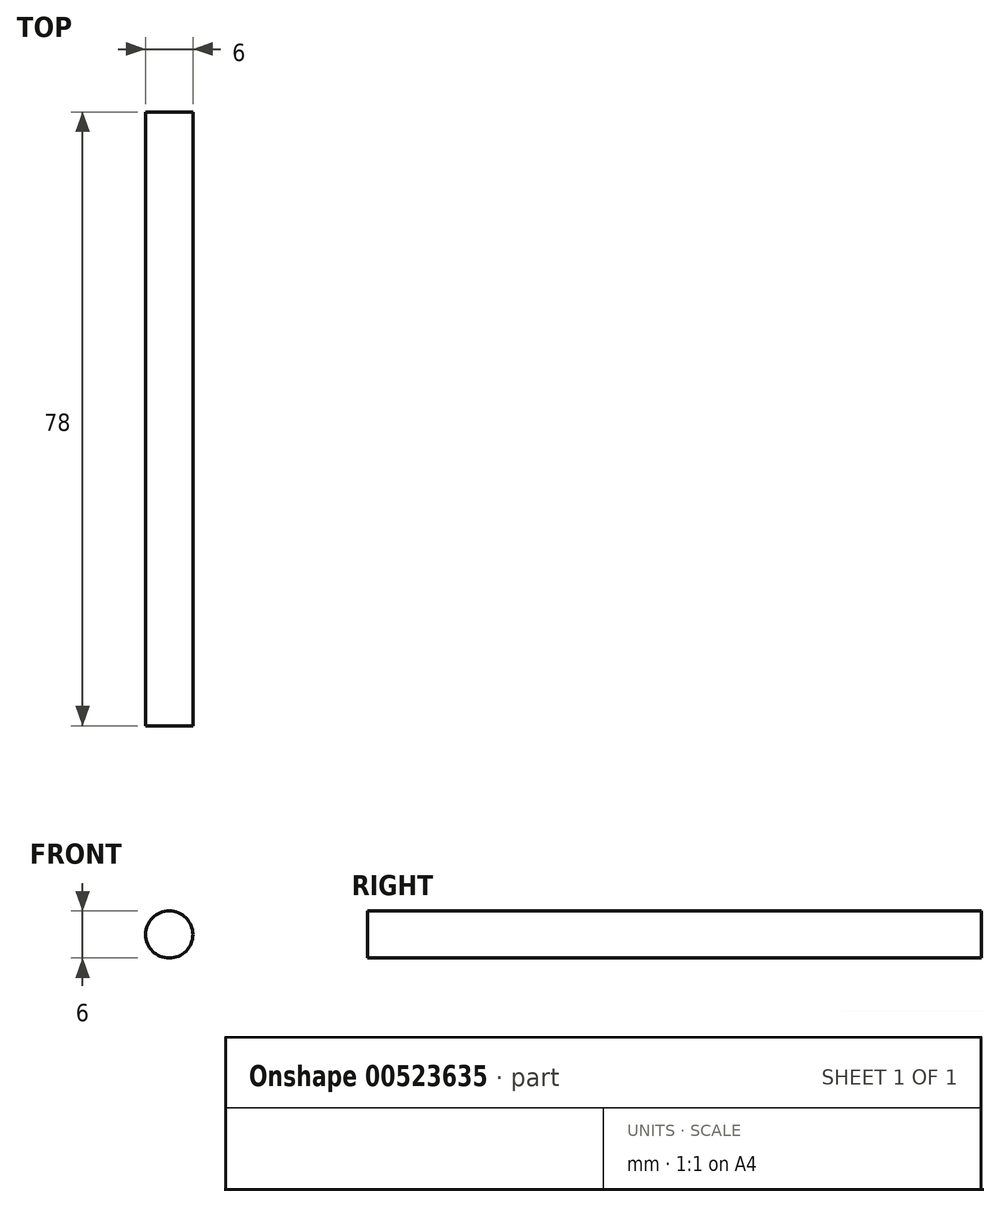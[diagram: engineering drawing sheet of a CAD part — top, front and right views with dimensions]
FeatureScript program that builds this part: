
annotation { "Feature Type Name" : "Feature", "Feature Type Description" : "" }
export const myFeature = defineFeature(function(context is Context, id is Id, definition is map)
    precondition{}
    {
        {
            var Q0;
            Q0=qCreatedBy(makeId("Front.planeOp"),FACE);
            var sketch = newSketch(context, id + "F0", { "sketchPlane" : qUnion([Q0])});
            skCircle(sketch, "E0", {"center": v(0, 0) * mm, "radius": 3 * mm});
            skSolve(sketch);
        }
        {
            var Q0;
            Q0 = qSketchRegion(id + "F0", true);
            extrude(context, id + "F1", {"entities" : qUnion([Q0]), "depth" : 78 * mm, "offsetDistance" : 25 * mm});
        }
        {
            var Q0;
            Q0=makeQuery(id+"F1.opExtrude","CAP_FACE",FACE,{"disambiguationData":[OSD([sQuery(id+"F0.wireOp",EDGE,"E0")])],"isStart":true});
            var Q1;
            Q1=makeQuery(id+"F1.opExtrude","CAP_FACE",FACE,{"disambiguationData":[OSD([sQuery(id+"F0.wireOp",EDGE,"E0")])],"isStart":false});
            cPlane(context, id + "F2", {"entities" : qUnion([Q0, Q1]), "cplaneType" : CPlaneType.MID_PLANE, "offset" : 25 * mm, "width" : 150 * mm, "height" : 150 * mm});
        }
    });
